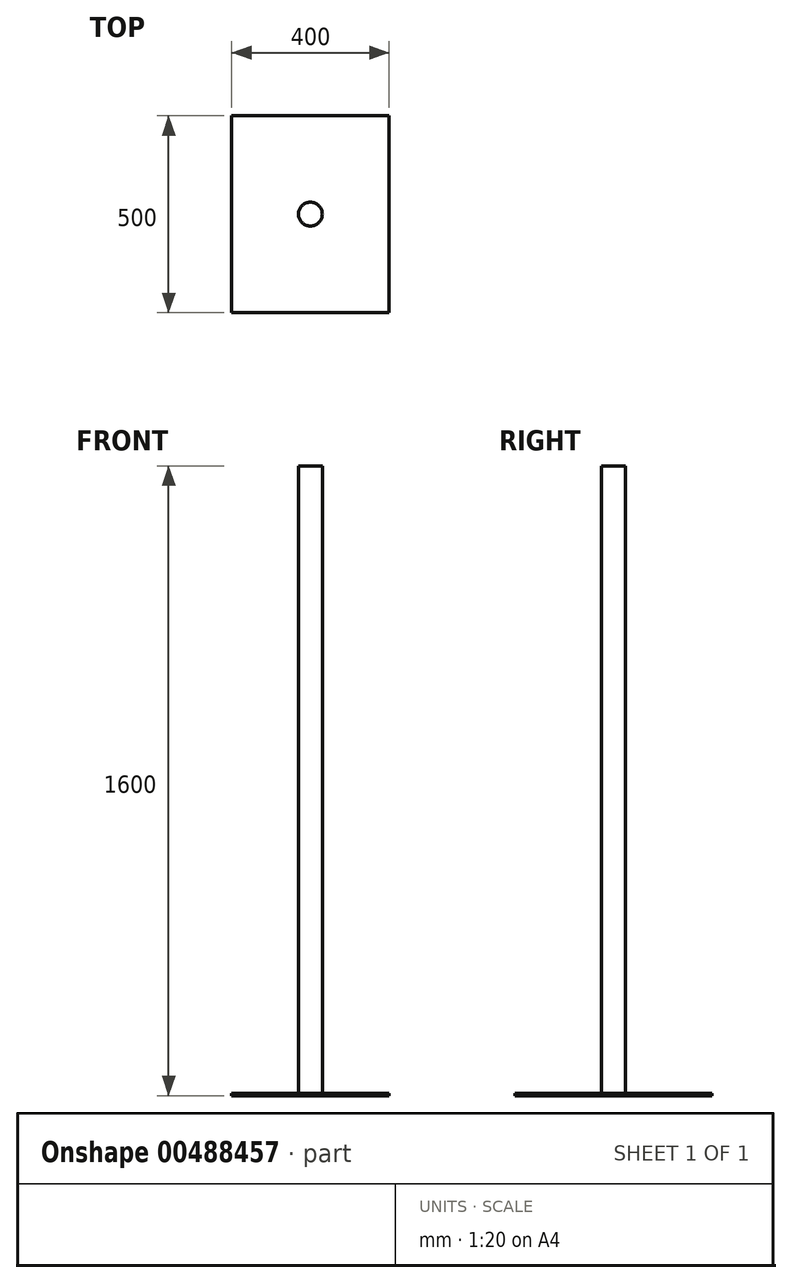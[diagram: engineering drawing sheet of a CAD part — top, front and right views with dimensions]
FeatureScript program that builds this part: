
annotation { "Feature Type Name" : "Feature", "Feature Type Description" : "" }
export const myFeature = defineFeature(function(context is Context, id is Id, definition is map)
    precondition{}
    {
        {
            var Q0;
            Q0=qCreatedBy(makeId("Top.planeOp"),FACE);
            var sketch = newSketch(context, id + "F0", { "sketchPlane" : qUnion([Q0])});
            skLineSegment(sketch, "E0.bottom", {"start": v(200, -250) * mm, "end": v(-200, -250) * mm});
            skLineSegment(sketch, "E0.top", {"start": v(200, 250) * mm, "end": v(-200, 250) * mm});
            skLineSegment(sketch, "E0.left", {"start": v(200, -250) * mm, "end": v(200, 250) * mm});
            skLineSegment(sketch, "E0.right", {"start": v(-200, -250) * mm, "end": v(-200, 250) * mm});
            skPoint(sketch, "E0.middle", {"position": v(0, 0) * mm});
            skSolve(sketch);
        }
        {
            var Q0;
            Q0 = qSketchRegion(id + "F0", true);
            extrude(context, id + "F1", {"entities" : qUnion([Q0]), "depth" : 6 * mm});
        }
        {
            var Q0;
            Q0=qCreatedBy(makeId("Top.planeOp"),FACE);
            var sketch = newSketch(context, id + "F2", { "sketchPlane" : qUnion([Q0])});
            skCircle(sketch, "E1", {"center": v(0, 0) * mm, "radius": 30.25 * mm});
            skSolve(sketch);
        }
        {
            var Q0;
            Q0 = qSketchRegion(id + "F2", true);
            extrude(context, id + "F3", {"entities" : qUnion([Q0]), "operationType" : NewBodyOperationType.ADD, "depth" : 1600 * mm});
        }
        {
            var Q0;
            Q0=qCreatedBy(makeId("Top.planeOp"),FACE);
            var sketch = newSketch(context, id + "F4", { "sketchPlane" : qUnion([Q0])});
            skLineSegment(sketch, "E2.bottom", {"start": v(75, 75) * mm, "end": v(-75, 75) * mm, "construction": true});
            skLineSegment(sketch, "E2.top", {"start": v(75, -75) * mm, "end": v(-75, -75) * mm, "construction": true});
            skLineSegment(sketch, "E2.left", {"start": v(75, 75) * mm, "end": v(75, -75) * mm, "construction": true});
            skLineSegment(sketch, "E2.right", {"start": v(-75, 75) * mm, "end": v(-75, -75) * mm, "construction": true});
            skPoint(sketch, "E2.middle", {"position": v(0, 0) * mm});
            skLineSegment(sketch, "E3", {"start": v(-75, 75) * mm, "end": v(75, -75) * mm, "construction": true});
            skLineSegment(sketch, "E4", {"start": v(75, 75) * mm, "end": v(-75, -75) * mm, "construction": true});
            skSolve(sketch);
        }
    });
